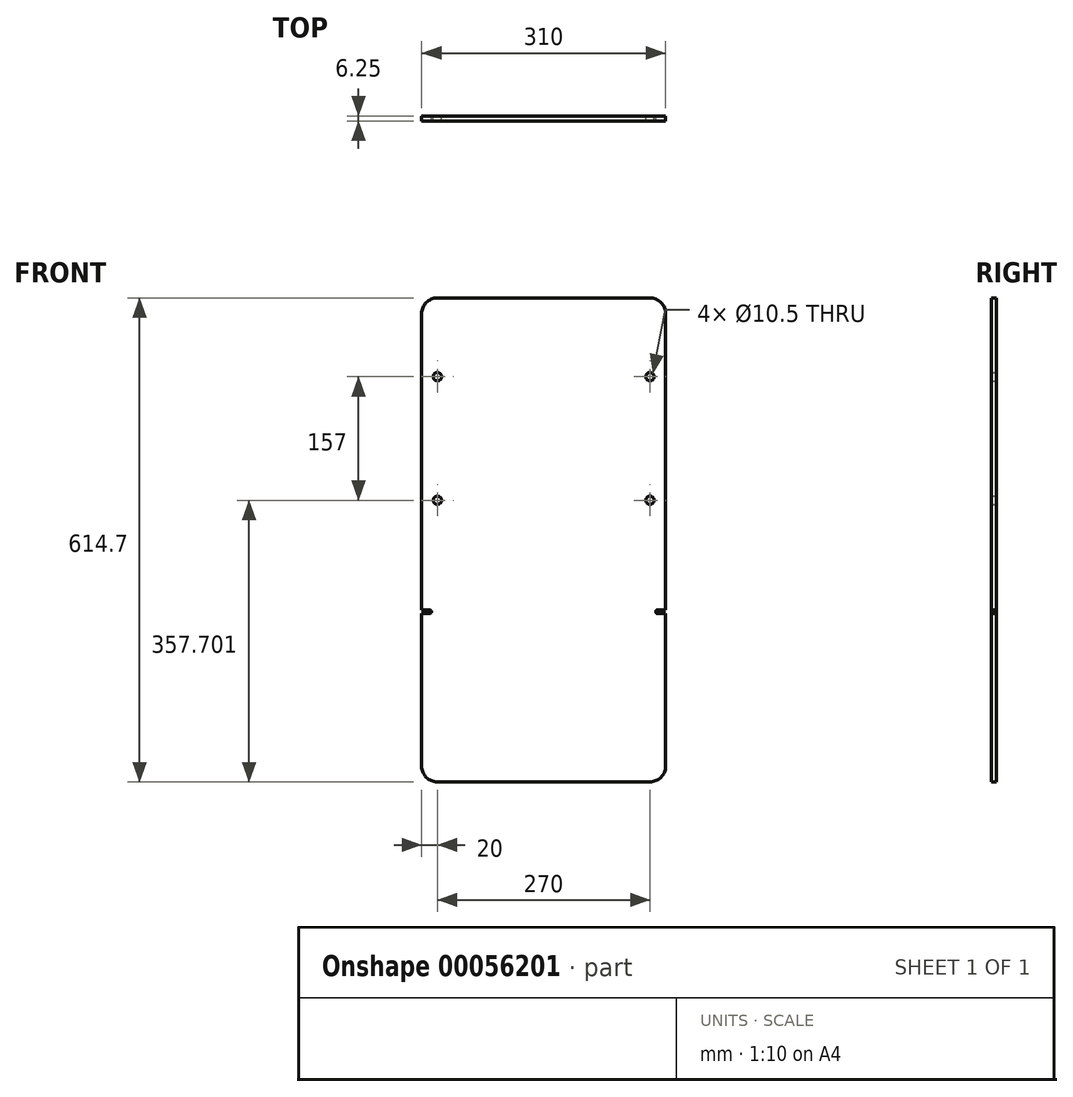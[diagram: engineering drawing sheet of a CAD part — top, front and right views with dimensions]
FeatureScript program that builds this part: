
annotation { "Feature Type Name" : "Feature", "Feature Type Description" : "" }
export const myFeature = defineFeature(function(context is Context, id is Id, definition is map)
    precondition{}
    {
        {
            var Q0;
            Q0=qCreatedBy(makeId("Front.planeOp"),FACE);
            var sketch = newSketch(context, id + "F0", { "sketchPlane" : qUnion([Q0])});
            skLineSegment(sketch, "E0", {"start": v(0, -337.26) * mm, "end": v(0, 61.32) * mm});
            skLineSegment(sketch, "E1.0", {"start": v(155, -533.38) * mm, "end": v(155, -339.76) * mm});
            skLineSegment(sketch, "E2", {"start": v(0, 61.32) * mm, "end": v(135, 61.32) * mm});
            skLineSegment(sketch, "E3.0", {"start": v(0, -38.68) * mm, "end": v(155, -38.68) * mm});
            skLineSegment(sketch, "E4.0", {"start": v(135, -337.26) * mm, "end": v(135, 62.74) * mm});
            skCircle(sketch, "E5", {"center": v(135, -38.68) * mm, "radius": 5.25 * mm});
            skLineSegment(sketch, "E6.0", {"start": v(0, -195.68) * mm, "end": v(155, -195.68) * mm});
            skCircle(sketch, "E7", {"center": v(135, -195.68) * mm, "radius": 5.25 * mm});
            skLineSegment(sketch, "E8.MirrorCS", {"start": v(0, 61.32) * mm, "end": v(-135, 61.32) * mm});
            skLineSegment(sketch, "E9.MirrorCS", {"start": v(-155, -533.38) * mm, "end": v(-155, -339.76) * mm});
            skCircle(sketch, "E10.MirrorC", {"center": v(-135, -195.68) * mm, "radius": 5.25 * mm});
            skCircle(sketch, "E11.MirrorC", {"center": v(-135, -38.68) * mm, "radius": 5.25 * mm});
            skPoint(sketch, "E12.visualSharp", {"position": v(-155, 61.32) * mm});
            skArc(sketch, "E12.filletArc", {"start": v(-135, 61.32) * mm, "mid": v(-149.14, 55.46) * mm, "end": v(-155, 41.32) * mm});
            skPoint(sketch, "E13.visualSharp", {"position": v(155, 61.32) * mm});
            skArc(sketch, "E13.filletArc", {"start": v(155, 41.32) * mm, "mid": v(149.14, 55.46) * mm, "end": v(135, 61.32) * mm});
            skLineSegment(sketch, "E14.0", {"start": v(135, -553.38) * mm, "end": v(-135, -553.38) * mm});
            skPoint(sketch, "E15.visualSharp", {"position": v(-155, -553.38) * mm});
            skArc(sketch, "E15.filletArc", {"start": v(-155, -533.38) * mm, "mid": v(-149.14, -547.52) * mm, "end": v(-135, -553.38) * mm});
            skPoint(sketch, "E16.visualSharp", {"position": v(155, -553.38) * mm});
            skArc(sketch, "E16.filletArc", {"start": v(135, -553.38) * mm, "mid": v(149.14, -547.52) * mm, "end": v(155, -533.38) * mm});
            skLineSegment(sketch, "E17.0", {"start": v(-145, -334.76) * mm, "end": v(-155, -334.76) * mm});
            skLineSegment(sketch, "E18.0", {"start": v(-145, -339.76) * mm, "end": v(-155, -339.76) * mm});
            skArc(sketch, "E19", {"start": v(-145, -339.76) * mm, "mid": v(-142.5, -337.26) * mm, "end": v(-145, -334.76) * mm});
            skPoint(sketch, "E20.orphan", {"position": v(-155, -337.26) * mm});
            skLineSegment(sketch, "E21.trimOffspring", {"start": v(-155, -334.76) * mm, "end": v(-155, 41.32) * mm});
            skPoint(sketch, "E22.MirrorCS.start.orphan", {"position": v(0, -337.26) * mm});
            skLineSegment(sketch, "E23.MirrorCS", {"start": v(145, -334.76) * mm, "end": v(155, -334.76) * mm});
            skLineSegment(sketch, "E24.MirrorCS", {"start": v(145, -339.76) * mm, "end": v(155, -339.76) * mm});
            skArc(sketch, "E25.MirrorCS", {"start": v(145, -339.76) * mm, "mid": v(142.5, -337.26) * mm, "end": v(145, -334.76) * mm});
            skPoint(sketch, "E26.orphan", {"position": v(155, -337.26) * mm});
            skLineSegment(sketch, "E27.trimOffspring", {"start": v(155, -334.76) * mm, "end": v(155, 41.32) * mm});
            skLineSegment(sketch, "E28", {"start": v(0, -337.26) * mm, "end": v(135, -337.26) * mm});
            skSolve(sketch);
        }
        {
            var Q0;
            Q0 = qSketchRegion(id + "F0", true);
            var Q1;
            {var subQ1=sQuery(id+"F0.wireOp",EDGE,"E3.0");var subQ5=sQuery(id+"F0.wireOp",EDGE,"E0");var subQ6=makeQuery(id+"F0.imprint","INTERSECT",VERTEX,{"derivedFrom":[subQ5,subQ1]});Q1=makeQuery(id+"F0.imprint","IMPRINT",FACE,{"disambiguationData":[TD([[makeQuery(id+"F0.imprint","IMPRINT",EDGE,{"disambiguationData":[TD([[subQ6,1.0]])],"derivedFrom":subQ5}),-1.0]])]});}
            var Q2;
            {var subQ5=sQuery(id+"F0.wireOp",EDGE,"E28");Q2=makeQuery(id+"F0.imprint","IMPRINT",FACE,{"disambiguationData":[TD([[makeQuery(id+"F0.imprint","IMPRINT",EDGE,{"derivedFrom":subQ5}),1.0]])]});}
            extrude(context, id + "F1", {"entities" : qUnion([Q0, Q1, Q2]), "depth" : 6.25 * mm});
        }
    });
